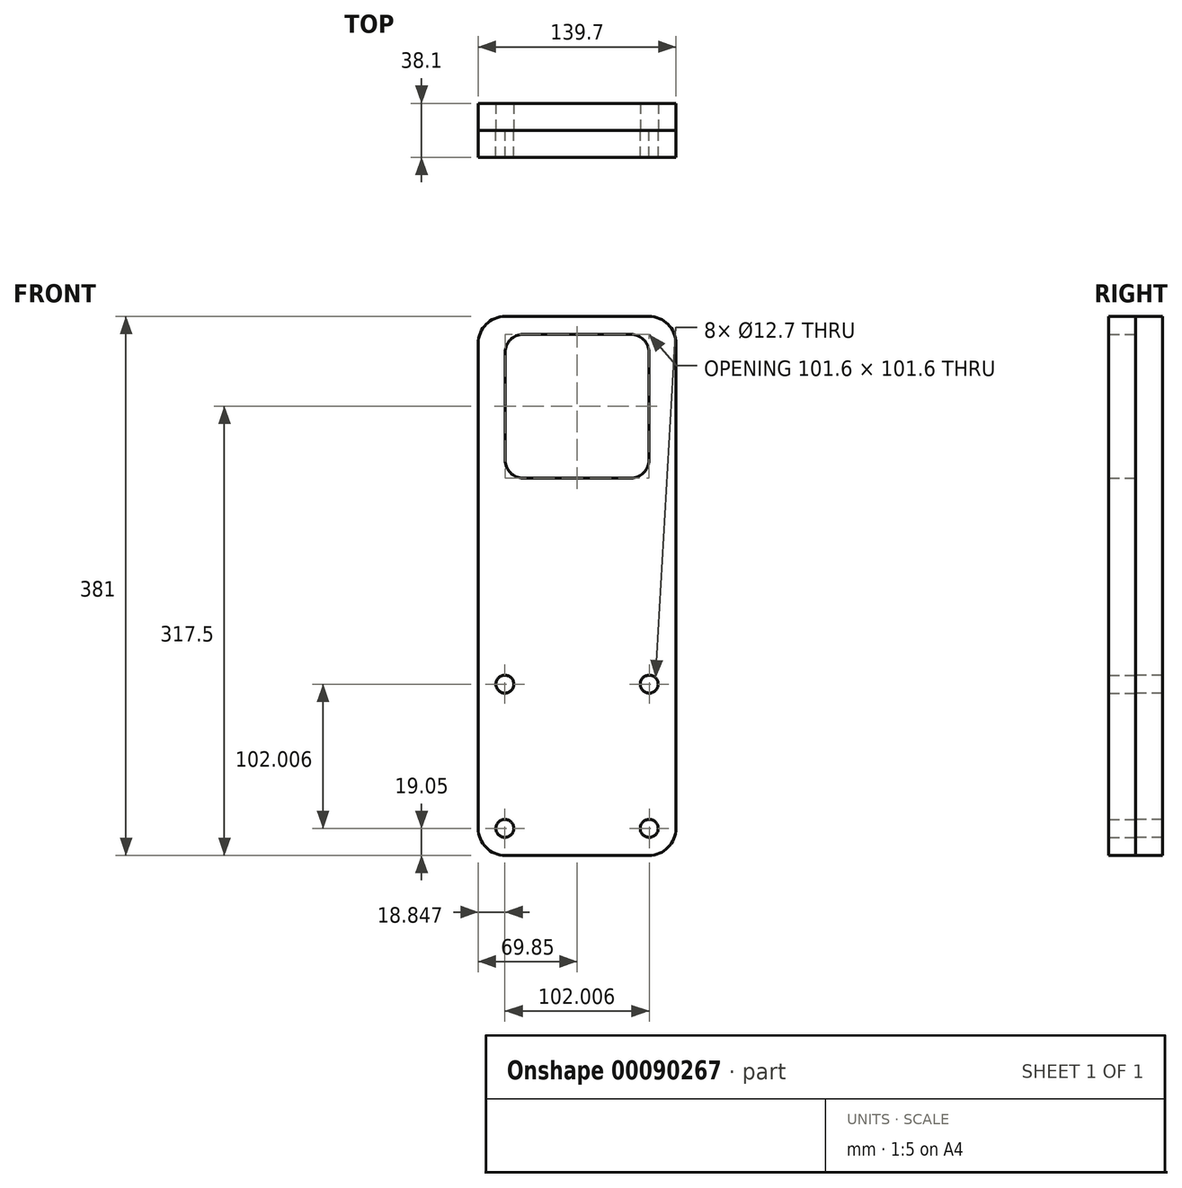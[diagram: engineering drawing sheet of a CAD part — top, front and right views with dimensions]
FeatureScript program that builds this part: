
annotation { "Feature Type Name" : "Feature", "Feature Type Description" : "" }
export const myFeature = defineFeature(function(context is Context, id is Id, definition is map)
    precondition{}
    {
        {
            var Q0;
            Q0=qCreatedBy(makeId("Front.planeOp"),FACE);
            var sketch = newSketch(context, id + "F0", { "sketchPlane" : qUnion([Q0])});
            skLineSegment(sketch, "E0.bottom", {"start": v(19.05, 0) * mm, "end": v(120.65, 0) * mm});
            skLineSegment(sketch, "E0.top", {"start": v(19.05, -381) * mm, "end": v(120.65, -381) * mm});
            skLineSegment(sketch, "E0.left", {"start": v(0, -19.05) * mm, "end": v(0, -361.95) * mm});
            skLineSegment(sketch, "E0.right", {"start": v(139.7, -19.05) * mm, "end": v(139.7, -361.95) * mm});
            skCircle(sketch, "E1", {"center": v(18.85, -361.95) * mm, "radius": 6.35 * mm});
            skLineSegment(sketch, "E2", {"start": v(69.85, 0) * mm, "end": v(69.85, -381) * mm, "construction": true});
            skCircle(sketch, "E3.0.1.0", {"center": v(18.85, -259.94) * mm, "radius": 6.35 * mm});
            skCircle(sketch, "E3.1.0.0", {"center": v(120.85, -361.95) * mm, "radius": 6.35 * mm});
            skCircle(sketch, "E3.1.1.0", {"center": v(120.85, -259.94) * mm, "radius": 6.35 * mm});
            skLineSegment(sketch, "E3.direction1", {"start": v(18.85, -361.95) * mm, "end": v(120.85, -361.95) * mm, "construction": true});
            skLineSegment(sketch, "E3.direction2", {"start": v(18.85, -361.95) * mm, "end": v(18.85, -259.94) * mm, "construction": true});
            skPoint(sketch, "E4.visualSharp", {"position": v(139.7, 0) * mm});
            skArc(sketch, "E4.filletArc", {"start": v(139.7, -19.05) * mm, "mid": v(134.12, -5.58) * mm, "end": v(120.65, 0) * mm});
            skPoint(sketch, "E5.visualSharp", {"position": v(139.7, -381) * mm});
            skArc(sketch, "E5.filletArc", {"start": v(120.65, -381) * mm, "mid": v(134.12, -375.42) * mm, "end": v(139.7, -361.95) * mm});
            skPoint(sketch, "E6.visualSharp", {"position": v(0, -381) * mm});
            skArc(sketch, "E6.filletArc", {"start": v(0, -361.95) * mm, "mid": v(5.58, -375.42) * mm, "end": v(19.05, -381) * mm});
            skPoint(sketch, "E7.visualSharp", {"position": v(0, 0) * mm});
            skArc(sketch, "E7.filletArc", {"start": v(19.05, 0) * mm, "mid": v(5.58, -5.58) * mm, "end": v(0, -19.05) * mm});
            skLineSegment(sketch, "E8.bottom", {"start": v(31.75, -12.7) * mm, "end": v(107.95, -12.7) * mm});
            skLineSegment(sketch, "E8.top", {"start": v(31.75, -114.3) * mm, "end": v(107.95, -114.3) * mm});
            skLineSegment(sketch, "E8.left", {"start": v(19.05, -25.4) * mm, "end": v(19.05, -101.6) * mm});
            skLineSegment(sketch, "E8.right", {"start": v(120.65, -25.4) * mm, "end": v(120.65, -101.6) * mm});
            skPoint(sketch, "E9", {"position": v(69.85, -114.3) * mm});
            skPoint(sketch, "E10.visualSharp", {"position": v(120.65, -12.7) * mm});
            skArc(sketch, "E10.filletArc", {"start": v(120.65, -25.4) * mm, "mid": v(116.93, -16.42) * mm, "end": v(107.95, -12.7) * mm});
            skPoint(sketch, "E11.visualSharp", {"position": v(120.65, -114.3) * mm});
            skArc(sketch, "E11.filletArc", {"start": v(107.95, -114.3) * mm, "mid": v(116.93, -110.58) * mm, "end": v(120.65, -101.6) * mm});
            skPoint(sketch, "E12.visualSharp", {"position": v(19.05, -114.3) * mm});
            skArc(sketch, "E12.filletArc", {"start": v(19.05, -101.6) * mm, "mid": v(22.77, -110.58) * mm, "end": v(31.75, -114.3) * mm});
            skPoint(sketch, "E13.visualSharp", {"position": v(19.05, -12.7) * mm});
            skArc(sketch, "E13.filletArc", {"start": v(31.75, -12.7) * mm, "mid": v(22.77, -16.42) * mm, "end": v(19.05, -25.4) * mm});
            skSolve(sketch);
        }
        {
            var Q0;
            Q0=makeQuery(id+"F0.imprint","IMPRINT",FACE,{"disambiguationData":[TD([[makeQuery(id+"F0.imprint","IMPRINT",EDGE,{"derivedFrom":sQuery(id+"F0.wireOp",EDGE,"E0.bottom")}),-1.0]])]});
            extrude(context, id + "F1", {"entities" : qUnion([Q0]), "depth" : 19.05 * mm});
        }
        {
            var Q0;
            Q0=makeQuery(id+"F0.imprint","IMPRINT",FACE,{"disambiguationData":[TD([[makeQuery(id+"F0.imprint","IMPRINT",EDGE,{"derivedFrom":sQuery(id+"F0.wireOp",EDGE,"E8.bottom")}),-1.0]])]});
            var Q1;
            Q1=makeQuery(id+"F0.imprint","IMPRINT",FACE,{"disambiguationData":[TD([[makeQuery(id+"F0.imprint","IMPRINT",EDGE,{"derivedFrom":sQuery(id+"F0.wireOp",EDGE,"E0.bottom")}),-1.0]])]});
            extrude(context, id + "F2", {"entities" : qUnion([Q0, Q1]), "oppositeDirection" : true, "depth" : 19.05 * mm});
        }
    });
